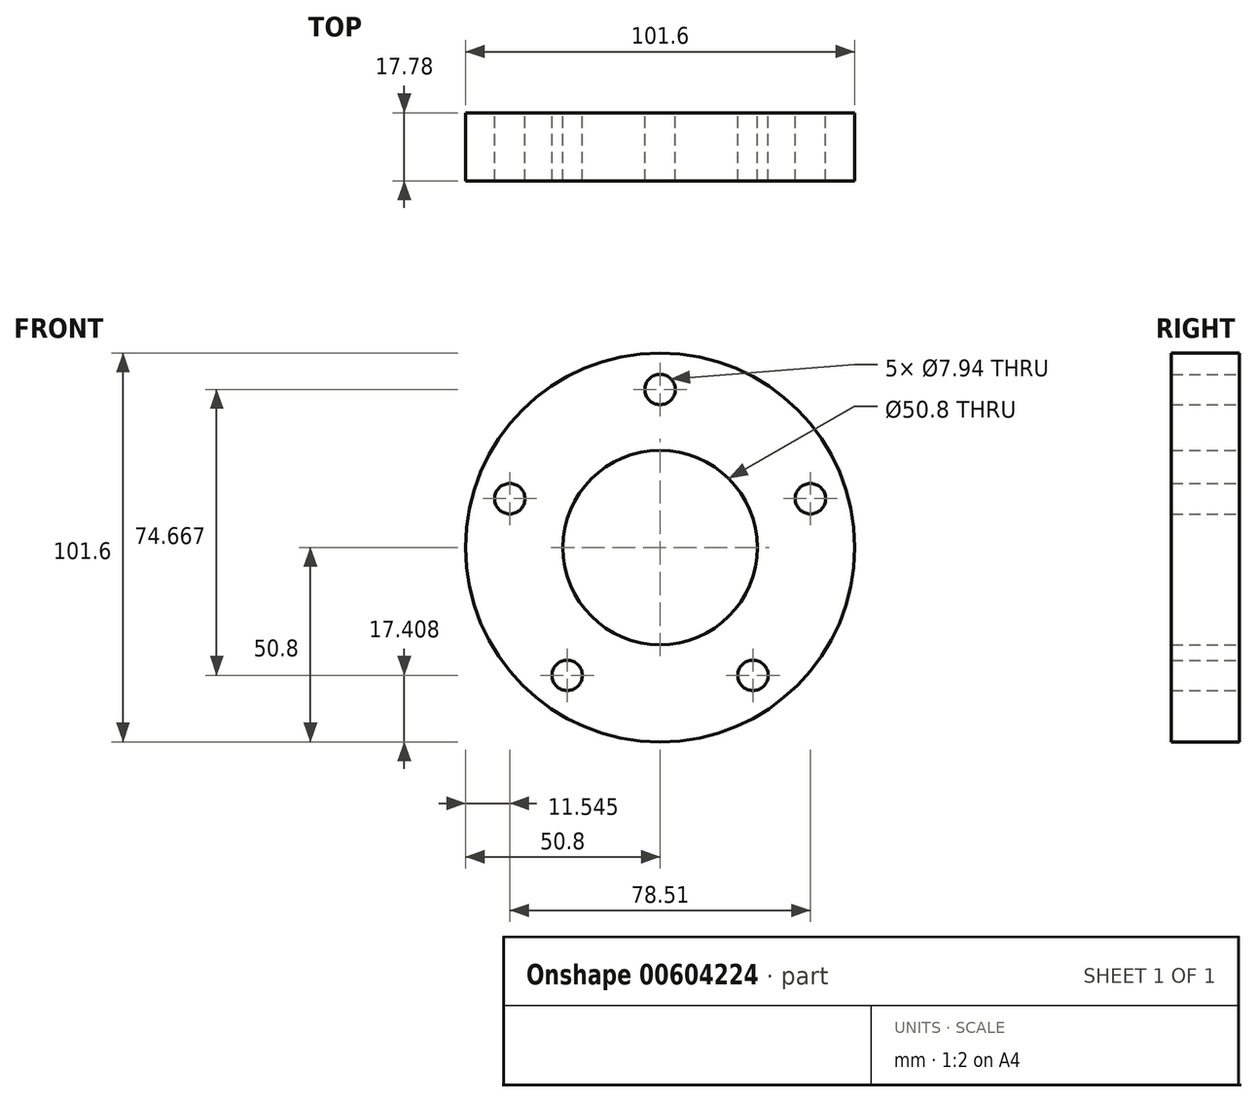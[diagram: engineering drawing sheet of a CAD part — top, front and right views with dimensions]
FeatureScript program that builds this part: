
annotation { "Feature Type Name" : "Feature", "Feature Type Description" : "" }
export const myFeature = defineFeature(function(context is Context, id is Id, definition is map)
    precondition{}
    {
        {
            var Q0;
            Q0=qCreatedBy(makeId("Front.planeOp"),FACE);
            var sketch = newSketch(context, id + "F0", { "sketchPlane" : qUnion([Q0])});
            skCircle(sketch, "E0", {"center": v(0, 0) * mm, "radius": 25.4 * mm});
            skCircle(sketch, "E1", {"center": v(0, 0) * mm, "radius": 50.8 * mm});
            skCircle(sketch, "E2", {"center": v(0, 0) * mm, "radius": 41.28 * mm});
            skLineSegment(sketch, "E3", {"start": v(0, 41.28) * mm, "end": v(0, 0) * mm});
            skLineSegment(sketch, "E4", {"start": v(0, 0) * mm, "end": v(39.25, 12.75) * mm});
            skLineSegment(sketch, "E5", {"start": v(0, 0) * mm, "end": v(24.26, -33.4) * mm});
            skLineSegment(sketch, "E6", {"start": v(0, 0) * mm, "end": v(-24.26, -33.4) * mm});
            skLineSegment(sketch, "E7", {"start": v(0, 0) * mm, "end": v(-39.25, 12.75) * mm});
            skPoint(sketch, "E8", {"position": v(0, 41.28) * mm});
            skPoint(sketch, "E9", {"position": v(-39.25, 12.75) * mm});
            skPoint(sketch, "E10", {"position": v(-24.26, -33.4) * mm});
            skPoint(sketch, "E11", {"position": v(24.26, -33.4) * mm});
            skPoint(sketch, "E12", {"position": v(39.25, 12.75) * mm});
            skSolve(sketch);
        }
        {
            var Q0;
            Q0=makeQuery(id+"F0.imprint","IMPRINT",FACE,{"disambiguationData":[TD([[makeQuery(id+"F0.imprint","IMPRINT",EDGE,{"derivedFrom":sQuery(id+"F0.wireOp",EDGE,"E1")}),1.0]])]});
            var Q1;
            {var subQ0=sQuery(id+"F0.wireOp",EDGE,"E3");var subQ1=sQuery(id+"F0.wireOp",EDGE,"E0");var subQ2=makeQuery(id+"F0.imprint","INTERSECT",VERTEX,{"derivedFrom":[subQ1,subQ0]});Q1=makeQuery(id+"F0.imprint","IMPRINT",FACE,{"disambiguationData":[TD([[makeQuery(id+"F0.imprint","IMPRINT",EDGE,{"disambiguationData":[TD([[subQ2,1.0]])],"derivedFrom":subQ1}),-1.0]])]});}
            var Q2;
            {var subQ0=sQuery(id+"F0.wireOp",EDGE,"E3");var subQ1=sQuery(id+"F0.wireOp",EDGE,"E0");var subQ2=makeQuery(id+"F0.imprint","INTERSECT",VERTEX,{"derivedFrom":[subQ1,subQ0]});Q2=makeQuery(id+"F0.imprint","IMPRINT",FACE,{"disambiguationData":[TD([[makeQuery(id+"F0.imprint","IMPRINT",EDGE,{"disambiguationData":[TD([[subQ2,-1.0]])],"derivedFrom":subQ1}),-1.0]])]});}
            var Q3;
            {var subQ0=sQuery(id+"F0.wireOp",EDGE,"E7");var subQ1=sQuery(id+"F0.wireOp",EDGE,"E0");var subQ2=makeQuery(id+"F0.imprint","INTERSECT",VERTEX,{"derivedFrom":[subQ1,subQ0]});Q3=makeQuery(id+"F0.imprint","IMPRINT",FACE,{"disambiguationData":[TD([[makeQuery(id+"F0.imprint","IMPRINT",EDGE,{"disambiguationData":[TD([[subQ2,-1.0]])],"derivedFrom":subQ1}),-1.0]])]});}
            var Q4;
            {var subQ0=sQuery(id+"F0.wireOp",EDGE,"E4");var subQ1=sQuery(id+"F0.wireOp",EDGE,"E0");var subQ2=makeQuery(id+"F0.imprint","INTERSECT",VERTEX,{"derivedFrom":[subQ1,subQ0]});Q4=makeQuery(id+"F0.imprint","IMPRINT",FACE,{"disambiguationData":[TD([[makeQuery(id+"F0.imprint","IMPRINT",EDGE,{"disambiguationData":[TD([[subQ2,1.0]])],"derivedFrom":subQ1}),-1.0]])]});}
            var Q5;
            {var subQ0=sQuery(id+"F0.wireOp",EDGE,"E6");var subQ1=sQuery(id+"F0.wireOp",EDGE,"E0");var subQ2=makeQuery(id+"F0.imprint","INTERSECT",VERTEX,{"derivedFrom":[subQ1,subQ0]});Q5=makeQuery(id+"F0.imprint","IMPRINT",FACE,{"disambiguationData":[TD([[makeQuery(id+"F0.imprint","IMPRINT",EDGE,{"disambiguationData":[TD([[subQ2,-1.0]])],"derivedFrom":subQ1}),-1.0]])]});}
            extrude(context, id + "F1", {"entities" : qUnion([Q0, Q1, Q2, Q3, Q4, Q5]), "endBound" : BoundingType.SYMMETRIC, "depth" : 17.78 * mm, "offsetDistance" : 25.4 * mm});
        }
        {
            var Q0;
            Q0=sQuery(id+"F0.wireOp",VERTEX,"E8");
            var Q1;
            Q1=sQuery(id+"F0.wireOp",VERTEX,"E12");
            var Q2;
            Q2=sQuery(id+"F0.wireOp",VERTEX,"E11");
            var Q3;
            Q3=sQuery(id+"F0.wireOp",VERTEX,"E10");
            var Q4;
            Q4=sQuery(id+"F0.wireOp",VERTEX,"E9");
            var Q5;
            Q5=makeQuery(id+"F1.opExtrude","SWEPT_BODY",BODY,{"disambiguationData":[OSD([sQuery(id+"F0.wireOp",EDGE,"E0"),sQuery(id+"F0.wireOp",EDGE,"E1")])]});
            hole(context, id + "F2", {"style" : HoleStyle.SIMPLE, "endStyle" : HoleEndStyle.THROUGH, "oppositeDirection" : true, "holeDiameter" : 7.94 * mm, "majorDiameter" : 6.35 * mm, "isTappedThrough" : true, "tappedDepth" : 12.7 * mm, "tapClearance" : 3, "locations" : qUnion([Q0, Q1, Q2, Q3, Q4]), "scope" : qUnion([Q5])});
        }
        {
            var Q0;
            Q0=sQuery(id+"F0.wireOp",VERTEX,"E8");
            var Q1;
            Q1=sQuery(id+"F0.wireOp",VERTEX,"E12");
            var Q2;
            Q2=sQuery(id+"F0.wireOp",VERTEX,"E9");
            var Q3;
            Q3=sQuery(id+"F0.wireOp",VERTEX,"E10");
            var Q4;
            Q4=sQuery(id+"F0.wireOp",VERTEX,"E11");
            var Q5;
            Q5=makeQuery(id+"F1.opExtrude","SWEPT_BODY",BODY,{"disambiguationData":[OSD([sQuery(id+"F0.wireOp",EDGE,"E0"),sQuery(id+"F0.wireOp",EDGE,"E1")])]});
            hole(context, id + "F3", {"style" : HoleStyle.SIMPLE, "endStyle" : HoleEndStyle.THROUGH, "holeDiameter" : 7.94 * mm, "majorDiameter" : 6.35 * mm, "isTappedThrough" : true, "tappedDepth" : 12.7 * mm, "tapClearance" : 3, "locations" : qUnion([Q0, Q1, Q2, Q3, Q4]), "scope" : qUnion([Q5])});
        }
    });
